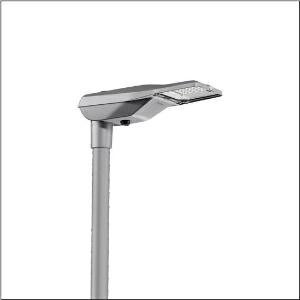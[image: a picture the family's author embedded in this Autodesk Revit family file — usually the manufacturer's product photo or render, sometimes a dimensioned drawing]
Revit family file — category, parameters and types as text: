
# Revit family: streetlight_sl_21_iq_micro___p0_5a_5xe1v31u08cb_845f
name_source: partatom
category: Lighting Fixtures
units: mm (PartAtom-declared; Revit-internal decimal feet)

## family parameters
Cut with Voids When Loaded = No
Host = Face
Light Source = No
Part Type = Normal
Room Calculation Point = No
Round Connector Dimension = Use Diameter
Shared = No

## types (1)
- --- (1 x LED, 2840 lm, 19.1 W, 3000K)
    Apparent Load = 19 VA
    CIE Flux Codes = 37 73 96 100 100
    Color Rendering = 70
    Color Temperature = 3000K
    Default Elevation = 1800 mm
    Description = Streetlight SL 21 iQ micro, mast luminaire, primary light control with lens, of PMMA, primary optical cover: cover, of toughened safety glass, transparent, light distribution: P0.5a, light emission: direct distribution, primary light characteristic: asymmetric, installation type: post-top, side-entry, LED, High Power LED, rated luminous flux: 2.840lm, luminous efficacy: 149lm/W, light colour: 730, colour temperature: 3000K, control gear: iQ-Street Remote, D4i with power reduction, control: pre-setting: logarithmic dimming characteristic, Street-Remote, Auto-Match, Temp-Guard, Lumen-Switch, Night-Set, Smart-Wire, Light-Fading, Desk-Remote (wireless, voltage-free reading and setting of iQ features in the workshop via application-optimized NFC function/RFID function), optimised constant luminous flux control (CLO 2.0), mains connection: 220..240V, AC, 50/60Hz, start of lifetime: 19W, end of service life: 20W, reduction: 9W, luminaire housing, of diecast aluminium, powder-coated, SITECO metallic grey (DB 702S), corrosivity category C5 high according to DIN EN ISO 12944, please order mast flange separately, inclination adjustable: 0°, 5°, 10°, 15°, sealing non-destructively replaceable, multi-level sealing system, length: 528mm, width: 235mm, height: 110mm, mast flange for spigot size: 42mm (side-entry): 5XC10008XM4, 60/48mm (side-entry/post-top): 5XC10108XM2, 76/60mm (side-entry/post-top): 5XC10108XM1, mounting height: 4..8m, Smart Interface below, protection rating (complete): IP66, insulation class (complete): insulation class II (safety insulation), certification: CE, ENEC, ENEC+, VDE, impact resistance: IK10, permissible operating ambient temperature for outdoor applications: -40..+50°C, standard-compliant lighting for roads and squares, packaging unit: 1 piece

Light Distribution: P0.5a
    Height = 110 mm
    Lamp = 1 x LED
    Lamp Light Flux = 2840 lm
    Lamp Power = 19.1 W
    Lamp count = 1
    Length = 528 mm
    Luminous efficacy = 149 lm/W
    Manufacturer = Siteco
    ModVariant = No
    Model = 5XE1V31U08CB
    Mounting Place = Pole
    Mounting Type = Pole top
    Number of Poles = 1
    OnlyDefault = Yes
    Power Factor = 1
    Product Name = Streetlight SL 21 iQ micro | P0.5a
    Product group = mast luminaire | pylon top
    ProductGroupID = 6100
    Protection Class = Protection class II
    Protection Degree = IP 66
    RLX_Detail_Level = 1
    RLX_Emergency_Light_Flux = 0 lm
    RLX_Emergency_Type = 0
    RLX_Emergency_Type_DB = No
    RlxData = <blob elided: 98533 chars, md5=a90289e1>
    Socket = socket
    Standby Power = 0 W
    System Light Flux = 2840 lm
    System Power = 19 W
    Type Comments = factory setting: luminous flux: 100 % | dim-lin: 254 | 387 mA
    Type Image = l_1277290.jpg
    URL = http://relux.com
    VarID = @adj_079559
    Voltage = 0 V
    Weight = 0.00 kg
    Width = 235 mm

## geometry (parser evidence)
native form markers: Blend x4, Sweep x10
no freeform markers — native parametric forms only
